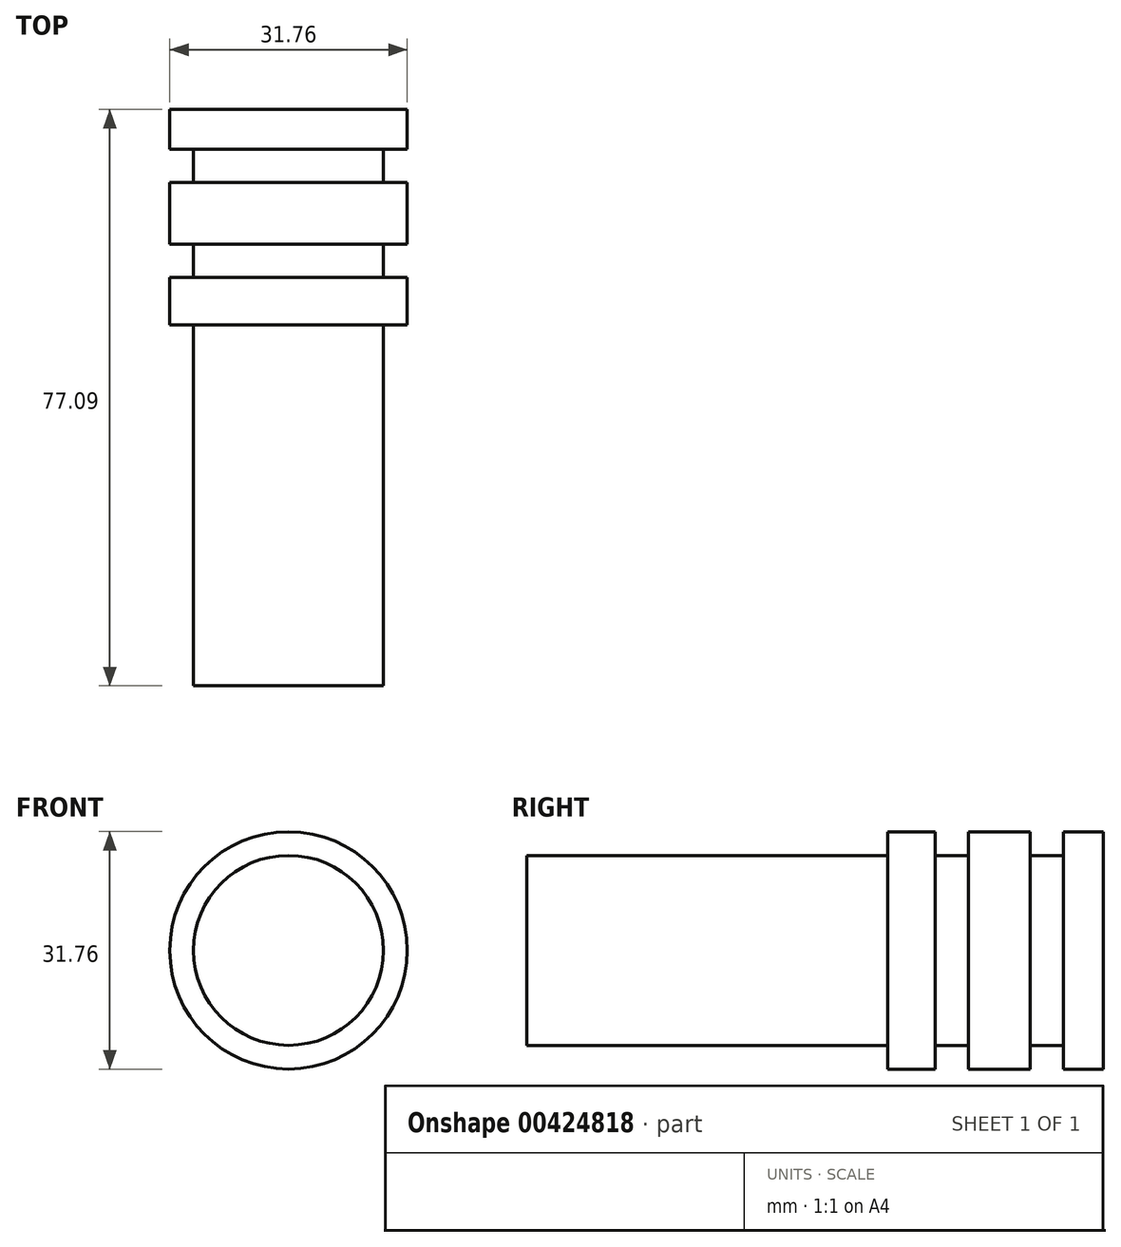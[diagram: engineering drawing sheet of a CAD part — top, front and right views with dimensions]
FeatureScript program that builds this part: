
annotation { "Feature Type Name" : "Feature", "Feature Type Description" : "" }
export const myFeature = defineFeature(function(context is Context, id is Id, definition is map)
    precondition{}
    {
        {
            var Q0;
            Q0=qCreatedBy(makeId("Front.planeOp"),FACE);
            var sketch = newSketch(context, id + "F0", { "sketchPlane" : qUnion([Q0])});
            skCircle(sketch, "E0", {"center": v(0, 0) * mm, "radius": 15.88 * mm});
            skSolve(sketch);
        }
        {
            var Q0;
            Q0 = qSketchRegion(id + "F0", true);
            extrude(context, id + "F1", {"entities" : qUnion([Q0]), "depth" : 5.33 * mm});
        }
        {
            var Q0;
            Q0=makeQuery(id+"F1.opExtrude","CAP_FACE",FACE,{"disambiguationData":[OSD([sQuery(id+"F0.wireOp",EDGE,"E0")])],"isStart":false});
            var sketch = newSketch(context, id + "F2", { "sketchPlane" : qUnion([Q0])});
            skCircle(sketch, "E1", {"center": v(0, 0) * mm, "radius": 12.7 * mm});
            skSolve(sketch);
        }
        {
            var Q0;
            Q0 = qSketchRegion(id + "F2", true);
            extrude(context, id + "F3", {"entities" : qUnion([Q0]), "operationType" : NewBodyOperationType.ADD, "depth" : 4.44 * mm});
        }
        {
            var Q0;
            Q0=makeQuery(id+"F3.opExtrude","CAP_FACE",FACE,{"disambiguationData":[OSD([sQuery(id+"F2.wireOp",EDGE,"E1")])],"isStart":false});
            var sketch = newSketch(context, id + "F4", { "sketchPlane" : qUnion([Q0])});
            skCircle(sketch, "E2.0", {"center": v(0, 0) * mm, "radius": 15.88 * mm});
            skSolve(sketch);
        }
        {
            var Q0;
            Q0 = qSketchRegion(id + "F4", true);
            extrude(context, id + "F5", {"entities" : qUnion([Q0]), "operationType" : NewBodyOperationType.ADD, "depth" : 8.25 * mm});
        }
        {
            var Q0;
            Q0=makeQuery(id+"F5.opExtrude","CAP_FACE",FACE,{"disambiguationData":[OSD([sQuery(id+"F4.wireOp",EDGE,"E2.0")])],"isStart":false});
            var sketch = newSketch(context, id + "F6", { "sketchPlane" : qUnion([Q0])});
            skCircle(sketch, "E3.0", {"center": v(0, 0) * mm, "radius": 12.7 * mm});
            skSolve(sketch);
        }
        {
            var Q0;
            Q0 = qSketchRegion(id + "F6", true);
            extrude(context, id + "F7", {"entities" : qUnion([Q0]), "operationType" : NewBodyOperationType.ADD, "depth" : 4.44 * mm});
        }
        {
            var Q0;
            Q0=makeQuery(id+"F7.opExtrude","CAP_FACE",FACE,{"disambiguationData":[OSD([sQuery(id+"F6.wireOp",EDGE,"E3.0")])],"isStart":false});
            var sketch = newSketch(context, id + "F8", { "sketchPlane" : qUnion([Q0])});
            skCircle(sketch, "E4.0", {"center": v(0, 0) * mm, "radius": 15.88 * mm});
            skSolve(sketch);
        }
        {
            var Q0;
            Q0 = qSketchRegion(id + "F8", true);
            extrude(context, id + "F9", {"entities" : qUnion([Q0]), "operationType" : NewBodyOperationType.ADD, "depth" : 6.35 * mm});
        }
        {
            var Q0;
            Q0=makeQuery(id+"F9.opExtrude","CAP_FACE",FACE,{"disambiguationData":[OSD([sQuery(id+"F8.wireOp",EDGE,"E4.0")])],"isStart":false});
            var sketch = newSketch(context, id + "F10", { "sketchPlane" : qUnion([Q0])});
            skCircle(sketch, "E5.0", {"center": v(0, 0) * mm, "radius": 12.7 * mm});
            skSolve(sketch);
        }
        {
            var Q0;
            Q0 = qSketchRegion(id + "F10", true);
            extrude(context, id + "F11", {"entities" : qUnion([Q0]), "operationType" : NewBodyOperationType.ADD, "depth" : 48.26 * mm});
        }
    });
